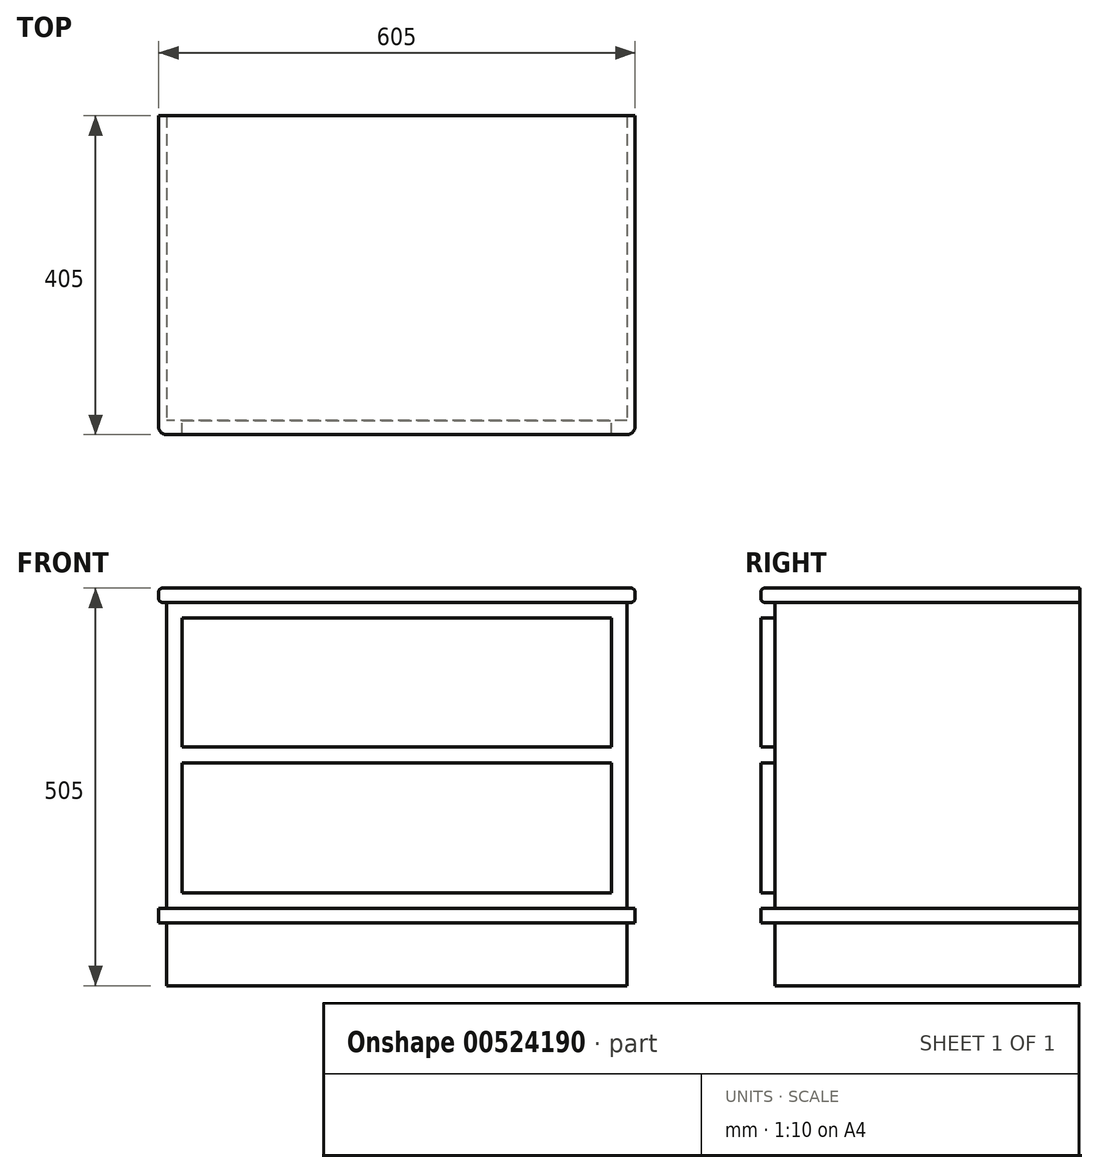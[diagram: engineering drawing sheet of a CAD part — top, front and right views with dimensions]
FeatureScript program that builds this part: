
annotation { "Feature Type Name" : "Feature", "Feature Type Description" : "" }
export const myFeature = defineFeature(function(context is Context, id is Id, definition is map)
    precondition{}
    {
        {
            var Q0;
            Q0=qCreatedBy(makeId("Top.planeOp"),FACE);
            var sketch = newSketch(context, id + "F0", { "sketchPlane" : qUnion([Q0])});
            skLineSegment(sketch, "E0.bottom", {"start": v(-605, 405) * mm, "end": v(0, 405) * mm});
            skLineSegment(sketch, "E0.top", {"start": v(-605, 0) * mm, "end": v(0, 0) * mm});
            skLineSegment(sketch, "E0.left", {"start": v(-605, 405) * mm, "end": v(-605, 0) * mm});
            skLineSegment(sketch, "E0.right", {"start": v(0, 405) * mm, "end": v(0, 0) * mm});
            skSolve(sketch);
        }
        {
            var Q0;
            Q0 = qSketchRegion(id + "F0", true);
            extrude(context, id + "F1", {"entities" : qUnion([Q0]), "depth" : 505 * mm, "offsetDistance" : 25 * mm});
        }
        {
            var Q0;
            Q0=makeQuery(id+"F1.opExtrude","SWEPT_FACE",FACE,{"disambiguationData":[OSD([sQuery(id+"F0.wireOp",EDGE,"E0.top")])]});
            var sketch = newSketch(context, id + "F2", { "sketchPlane" : qUnion([Q0])});
            skLineSegment(sketch, "E1.0", {"start": v(-605, 505) * mm, "end": v(-605, 0) * mm});
            skLineSegment(sketch, "E2.0", {"start": v(0, 505) * mm, "end": v(0, 0) * mm});
            skLineSegment(sketch, "E3.0", {"start": v(-605, 0) * mm, "end": v(0, 0) * mm});
            skLineSegment(sketch, "E4.0", {"start": v(-605, 505) * mm, "end": v(0, 505) * mm});
            skLineSegment(sketch, "E5.bottom", {"start": v(-605, 487) * mm, "end": v(-595, 487) * mm});
            skLineSegment(sketch, "E5.top", {"start": v(-605, 98) * mm, "end": v(-595, 98) * mm});
            skLineSegment(sketch, "E5.left", {"start": v(-605, 487) * mm, "end": v(-605, 98) * mm});
            skLineSegment(sketch, "E5.right", {"start": v(-595, 487) * mm, "end": v(-595, 98) * mm});
            skLineSegment(sketch, "E6.bottom", {"start": v(-605, 80) * mm, "end": v(-595, 80) * mm});
            skLineSegment(sketch, "E6.top", {"start": v(-605, 0) * mm, "end": v(-595, 0) * mm});
            skLineSegment(sketch, "E6.left", {"start": v(-605, 80) * mm, "end": v(-605, 0) * mm});
            skLineSegment(sketch, "E6.right", {"start": v(-595, 80) * mm, "end": v(-595, 0) * mm});
            skLineSegment(sketch, "E7.bottom", {"start": v(0, 487) * mm, "end": v(-10, 487) * mm});
            skLineSegment(sketch, "E7.top", {"start": v(0, 98) * mm, "end": v(-10, 98) * mm});
            skLineSegment(sketch, "E7.left", {"start": v(0, 487) * mm, "end": v(0, 98) * mm});
            skLineSegment(sketch, "E7.right", {"start": v(-10, 487) * mm, "end": v(-10, 98) * mm});
            skLineSegment(sketch, "E8.bottom", {"start": v(0, 80) * mm, "end": v(-10, 80) * mm});
            skLineSegment(sketch, "E8.top", {"start": v(0, 0) * mm, "end": v(-10, 0) * mm});
            skLineSegment(sketch, "E8.left", {"start": v(0, 80) * mm, "end": v(0, 0) * mm});
            skLineSegment(sketch, "E8.right", {"start": v(-10, 80) * mm, "end": v(-10, 0) * mm});
            skSolve(sketch);
        }
        {
            var Q0;
            {var subQ0=sQuery(id+"F2.wireOp",EDGE,"E5.bottom");Q0=makeQuery(id+"F2.imprint","IMPRINT",FACE,{"disambiguationData":[TD([[makeQuery(id+"F2.imprint","IMPRINT",EDGE,{"derivedFrom":subQ0}),-1.0]])]});}
            var Q1;
            {var subQ3=sQuery(id+"F2.wireOp",EDGE,"E6.bottom");Q1=makeQuery(id+"F2.imprint","IMPRINT",FACE,{"disambiguationData":[TD([[makeQuery(id+"F2.imprint","IMPRINT",EDGE,{"derivedFrom":subQ3}),-1.0]])]});}
            var Q2;
            {var subQ0=sQuery(id+"F2.wireOp",EDGE,"E7.bottom");Q2=makeQuery(id+"F2.imprint","IMPRINT",FACE,{"disambiguationData":[TD([[makeQuery(id+"F2.imprint","IMPRINT",EDGE,{"derivedFrom":subQ0}),1.0]])]});}
            var Q3;
            {var subQ3=sQuery(id+"F2.wireOp",EDGE,"E8.bottom");Q3=makeQuery(id+"F2.imprint","IMPRINT",FACE,{"disambiguationData":[TD([[makeQuery(id+"F2.imprint","IMPRINT",EDGE,{"derivedFrom":subQ3}),1.0]])]});}
            extrude(context, id + "F3", {"entities" : qUnion([Q0, Q1, Q2, Q3]), "operationType" : NewBodyOperationType.REMOVE, "oppositeDirection" : true, "depth" : 410 * mm, "offsetDistance" : 25 * mm});
        }
        {
            var Q0;
            Q0=makeQuery(id+"F3.boolean.opBoolean","COPY",FACE,{"derivedFrom":makeQuery(id+"F3.opExtrude","SWEPT_FACE",FACE,{"disambiguationData":[OSD([sQuery(id+"F2.wireOp",EDGE,"E5.right")])]})});
            var sketch = newSketch(context, id + "F4", { "sketchPlane" : qUnion([Q0])});
            skLineSegment(sketch, "E9.0", {"start": v(-405, 487) * mm, "end": v(0, 487) * mm});
            skLineSegment(sketch, "E10.0", {"start": v(-405, 98) * mm, "end": v(0, 98) * mm});
            skLineSegment(sketch, "E11.0", {"start": v(-405, 80) * mm, "end": v(0, 80) * mm});
            skLineSegment(sketch, "E12.0", {"start": v(-405, 0) * mm, "end": v(0, 0) * mm});
            skLineSegment(sketch, "E13.0", {"start": v(0, 487) * mm, "end": v(0, 98) * mm});
            skLineSegment(sketch, "E14.0", {"start": v(0, 80) * mm, "end": v(0, 0) * mm});
            skLineSegment(sketch, "E15.bottom", {"start": v(-18, 487) * mm, "end": v(0, 487) * mm});
            skLineSegment(sketch, "E15.top", {"start": v(-18, 98) * mm, "end": v(0, 98) * mm});
            skLineSegment(sketch, "E15.left", {"start": v(-18, 487) * mm, "end": v(-18, 98) * mm});
            skLineSegment(sketch, "E16.bottom", {"start": v(-18, 80) * mm, "end": v(0, 80) * mm});
            skLineSegment(sketch, "E16.top", {"start": v(-18, 0) * mm, "end": v(0, 0) * mm});
            skLineSegment(sketch, "E16.left", {"start": v(-18, 80) * mm, "end": v(-18, 0) * mm});
            skSolve(sketch);
        }
        {
            var Q0;
            {var subQ0=sQuery(id+"F4.wireOp",EDGE,"E13.0");Q0=makeQuery(id+"F4.imprint","IMPRINT",FACE,{"disambiguationData":[TD([[makeQuery(id+"F4.imprint","IMPRINT",EDGE,{"derivedFrom":subQ0}),-1.0]])]});}
            var Q1;
            {var subQ0=sQuery(id+"F4.wireOp",EDGE,"E14.0");Q1=makeQuery(id+"F4.imprint","IMPRINT",FACE,{"disambiguationData":[TD([[makeQuery(id+"F4.imprint","IMPRINT",EDGE,{"derivedFrom":subQ0}),-1.0]])]});}
            extrude(context, id + "F5", {"entities" : qUnion([Q0, Q1]), "operationType" : NewBodyOperationType.REMOVE, "oppositeDirection" : true, "depth" : 610 * mm, "offsetDistance" : 25 * mm});
        }
        {
            var Q0;
            Q0=makeQuery(id+"F1.opExtrude","CAP_FACE",FACE,{"disambiguationData":[OSD([sQuery(id+"F0.wireOp",EDGE,"E0.bottom"),sQuery(id+"F0.wireOp",EDGE,"E0.top"),sQuery(id+"F0.wireOp",EDGE,"E0.left"),sQuery(id+"F0.wireOp",EDGE,"E0.right")])],"isStart":false});
            var sketch = newSketch(context, id + "F6", { "sketchPlane" : qUnion([Q0])});
            skLineSegment(sketch, "E17.0", {"start": v(-605, 405) * mm, "end": v(-605, 0) * mm});
            skLineSegment(sketch, "E18.0", {"start": v(-605, 0) * mm, "end": v(-10, 0) * mm});
            skLineSegment(sketch, "E19.0", {"start": v(0, 405) * mm, "end": v(0, 10) * mm});
            skLineSegment(sketch, "E20", {"start": v(-665.06, 10) * mm, "end": v(98.12, 10) * mm, "construction": true});
            skLineSegment(sketch, "E21", {"start": v(-595, 101.75) * mm, "end": v(-595, -70.32) * mm, "construction": true});
            skLineSegment(sketch, "E22", {"start": v(-10, 81.04) * mm, "end": v(-10, -68.73) * mm, "construction": true});
            skArc(sketch, "E23", {"start": v(-605, 10) * mm, "mid": v(-602.07, 2.93) * mm, "end": v(-595, 0) * mm});
            skPoint(sketch, "E24.visualSharp", {"position": v(0, 0) * mm});
            skArc(sketch, "E24.filletArc", {"start": v(-10, 0) * mm, "mid": v(-2.93, 2.93) * mm, "end": v(0, 10) * mm});
            skSolve(sketch);
        }
        {
            var Q0;
            {var subQ3=sQuery(id+"F6.wireOp",EDGE,"E23");Q0=makeQuery(id+"F6.imprint","IMPRINT",FACE,{"disambiguationData":[TD([[makeQuery(id+"F6.imprint","IMPRINT",EDGE,{"derivedFrom":subQ3}),-1.0]])]});}
            var Q1;
            {var subQ0=sQuery(id+"F6.wireOp",EDGE,"E24.filletArc");Q1=makeQuery(id+"F6.imprint","IMPRINT",FACE,{"disambiguationData":[TD([[makeQuery(id+"F6.imprint","IMPRINT",EDGE,{"derivedFrom":subQ0}),-1.0]])]});}
            extrude(context, id + "F7", {"entities" : qUnion([Q0, Q1]), "operationType" : NewBodyOperationType.REMOVE, "oppositeDirection" : true, "depth" : 510 * mm, "offsetDistance" : 25 * mm});
        }
        {
            var Q0;
            Q0=makeQuery(id+"F1.opExtrude","CAP_EDGE",EDGE,{"disambiguationData":[OSD([sQuery(id+"F0.wireOp",EDGE,"E0.top")])],"isStart":false});
            var Q1;
            Q1=makeQuery(id+"F5.boolean.opBoolean","MERGE",EDGE,{"derivedFrom":[makeQuery(id+"F3.boolean.opBoolean","COPY",EDGE,{"derivedFrom":makeQuery(id+"F3.opExtrude","CAP_EDGE",EDGE,{"disambiguationData":[OSD([sQuery(id+"F2.wireOp",EDGE,"E5.bottom")])],"isStart":true})}),makeQuery(id+"F3.boolean.opBoolean","COPY",EDGE,{"derivedFrom":makeQuery(id+"F3.opExtrude","CAP_EDGE",EDGE,{"disambiguationData":[OSD([sQuery(id+"F2.wireOp",EDGE,"E7.bottom")])],"isStart":true})})],"fromTools":[makeQuery(id+"F5.opExtrude","SWEPT_EDGE",EDGE,{"disambiguationData":[OSD([sQuery(id+"F4.wireOp",EDGE,"E9.0"),sQuery(id+"F4.wireOp",EDGE,"E13.0")])]})]});
            var Q2;
            Q2=makeQuery(id+"F5.boolean.opBoolean","MERGE",EDGE,{"derivedFrom":[makeQuery(id+"F3.boolean.opBoolean","COPY",EDGE,{"derivedFrom":makeQuery(id+"F3.opExtrude","CAP_EDGE",EDGE,{"disambiguationData":[OSD([sQuery(id+"F2.wireOp",EDGE,"E5.top")])],"isStart":true})}),makeQuery(id+"F3.boolean.opBoolean","COPY",EDGE,{"derivedFrom":makeQuery(id+"F3.opExtrude","CAP_EDGE",EDGE,{"disambiguationData":[OSD([sQuery(id+"F2.wireOp",EDGE,"E7.top")])],"isStart":true})})],"fromTools":[makeQuery(id+"F5.opExtrude","SWEPT_EDGE",EDGE,{"disambiguationData":[OSD([sQuery(id+"F4.wireOp",EDGE,"E10.0"),sQuery(id+"F4.wireOp",EDGE,"E13.0")])]})]});
            var Q3;
            Q3=makeQuery(id+"F5.boolean.opBoolean","MERGE",EDGE,{"derivedFrom":[makeQuery(id+"F3.boolean.opBoolean","COPY",EDGE,{"derivedFrom":makeQuery(id+"F3.opExtrude","CAP_EDGE",EDGE,{"disambiguationData":[OSD([sQuery(id+"F2.wireOp",EDGE,"E6.bottom")])],"isStart":true})}),makeQuery(id+"F3.boolean.opBoolean","COPY",EDGE,{"derivedFrom":makeQuery(id+"F3.opExtrude","CAP_EDGE",EDGE,{"disambiguationData":[OSD([sQuery(id+"F2.wireOp",EDGE,"E8.bottom")])],"isStart":true})})],"fromTools":[makeQuery(id+"F5.opExtrude","SWEPT_EDGE",EDGE,{"disambiguationData":[OSD([sQuery(id+"F4.wireOp",EDGE,"E11.0"),sQuery(id+"F4.wireOp",EDGE,"E14.0")])]})]});
            fillet(context, id + "F8", {"entities" : qUnion([Q0, Q1, Q2, Q3]), "radius" : 5 * mm, "tangentPropagation" : true, "allowEdgeOverflow" : false});
        }
        {
            var Q0;
            Q0=makeQuery(id+"F5.boolean.opBoolean","COPY",FACE,{"derivedFrom":makeQuery(id+"F5.opExtrude","SWEPT_FACE",FACE,{"disambiguationData":[OSD([sQuery(id+"F4.wireOp",EDGE,"E15.left")])]})});
            var sketch = newSketch(context, id + "F9", { "sketchPlane" : qUnion([Q0])});
            skLineSegment(sketch, "E25.bottom", {"start": v(-575, 467) * mm, "end": v(-30, 467) * mm});
            skLineSegment(sketch, "E25.top", {"start": v(-575, 303) * mm, "end": v(-30, 303) * mm});
            skLineSegment(sketch, "E25.left", {"start": v(-575, 467) * mm, "end": v(-575, 303) * mm});
            skLineSegment(sketch, "E25.right", {"start": v(-30, 467) * mm, "end": v(-30, 303) * mm});
            skLineSegment(sketch, "E26.bottom", {"start": v(-575, 283) * mm, "end": v(-30, 283) * mm});
            skLineSegment(sketch, "E26.top", {"start": v(-575, 118) * mm, "end": v(-30, 118) * mm});
            skLineSegment(sketch, "E26.left", {"start": v(-575, 283) * mm, "end": v(-575, 118) * mm});
            skLineSegment(sketch, "E26.right", {"start": v(-30, 283) * mm, "end": v(-30, 118) * mm});
            skSolve(sketch);
        }
        {
            var Q0;
            Q0 = qSketchRegion(id + "F9", true);
            extrude(context, id + "F10", {"entities" : qUnion([Q0]), "operationType" : NewBodyOperationType.ADD, "depth" : 18 * mm, "offsetDistance" : 25 * mm});
        }
    });
